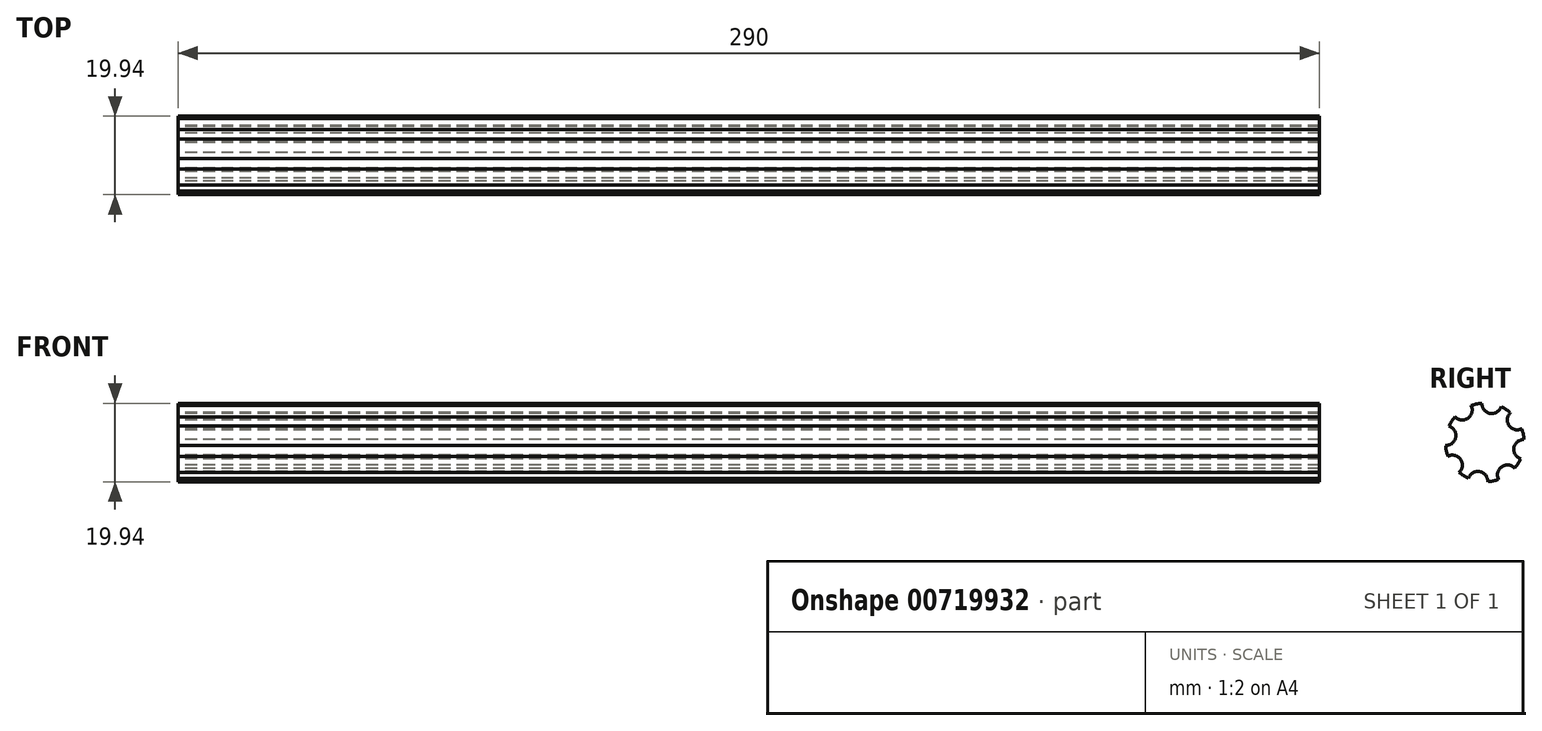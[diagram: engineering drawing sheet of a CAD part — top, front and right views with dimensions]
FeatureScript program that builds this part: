
annotation { "Feature Type Name" : "Feature", "Feature Type Description" : "" }
export const myFeature = defineFeature(function(context is Context, id is Id, definition is map)
    precondition{}
    {
        {
            var Q0;
            Q0=qCreatedBy(makeId("Right.planeOp"),FACE);
            var sketch = newSketch(context, id + "F0", { "sketchPlane" : qUnion([Q0])});
            skArc(sketch, "E0", {"start": v(7.57, -6.53) * mm, "mid": v(8.42, -5.4) * mm, "end": v(9.1, -4.15) * mm});
            skArc(sketch, "E1", {"start": v(7.57, -6.53) * mm, "mid": v(4.29, -6.15) * mm, "end": v(3.5, -9.37) * mm});
            skArc(sketch, "E2.1.0", {"start": v(9.97, 0.74) * mm, "mid": v(7.38, -1.32) * mm, "end": v(9.1, -4.15) * mm});
            skArc(sketch, "E2.2.0", {"start": v(6.53, 7.57) * mm, "mid": v(6.15, 4.29) * mm, "end": v(9.37, 3.5) * mm});
            skArc(sketch, "E2.3.0", {"start": v(-0.74, 9.97) * mm, "mid": v(1.32, 7.38) * mm, "end": v(4.15, 9.1) * mm});
            skArc(sketch, "E2.4.0", {"start": v(-7.57, 6.53) * mm, "mid": v(-4.29, 6.15) * mm, "end": v(-3.5, 9.37) * mm});
            skArc(sketch, "E2.5.0", {"start": v(-9.97, -0.74) * mm, "mid": v(-7.38, 1.32) * mm, "end": v(-9.1, 4.15) * mm});
            skArc(sketch, "E2.6.0", {"start": v(-6.53, -7.57) * mm, "mid": v(-6.15, -4.29) * mm, "end": v(-9.37, -3.5) * mm});
            skArc(sketch, "E2.7.0", {"start": v(0.74, -9.97) * mm, "mid": v(-1.32, -7.38) * mm, "end": v(-4.15, -9.1) * mm});
            skArc(sketch, "E3.trimOffspring", {"start": v(9.97, 0.74) * mm, "mid": v(9.77, 2.14) * mm, "end": v(9.37, 3.5) * mm});
            skArc(sketch, "E4.trimOffspring", {"start": v(6.53, 7.57) * mm, "mid": v(5.4, 8.42) * mm, "end": v(4.15, 9.1) * mm});
            skArc(sketch, "E5.trimOffspring", {"start": v(-0.74, 9.97) * mm, "mid": v(-2.14, 9.77) * mm, "end": v(-3.5, 9.37) * mm});
            skArc(sketch, "E6.trimOffspring", {"start": v(-7.57, 6.53) * mm, "mid": v(-8.42, 5.4) * mm, "end": v(-9.1, 4.15) * mm});
            skArc(sketch, "E7.trimOffspring", {"start": v(-9.97, -0.74) * mm, "mid": v(-9.77, -2.14) * mm, "end": v(-9.37, -3.5) * mm});
            skArc(sketch, "E8.trimOffspring", {"start": v(-6.53, -7.57) * mm, "mid": v(-5.4, -8.42) * mm, "end": v(-4.15, -9.1) * mm});
            skArc(sketch, "E9.trimOffspring", {"start": v(0.74, -9.97) * mm, "mid": v(2.14, -9.77) * mm, "end": v(3.5, -9.37) * mm});
            skSolve(sketch);
        }
        {
            var Q0;
            Q0 = qSketchRegion(id + "F0", true);
            extrude(context, id + "F1", {"entities" : qUnion([Q0]), "depth" : 290 * mm, "offsetDistance" : 25 * mm});
        }
    });
